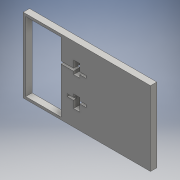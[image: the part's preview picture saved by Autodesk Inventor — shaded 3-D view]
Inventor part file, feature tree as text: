
AUTODESK INVENTOR PART (.ipt)
format: ipt  version: 2016 (Build 200138000, 138)  size: 164,864 bytes
history: native  units: mm
features: extrude x2, sketch x2
ambient origin geometry x8: Origin, YZ Plane, XZ Plane, XY Plane, X Axis, Y Axis, Z Axis, Center Point
bodies: Solid1 (feature_tree)
feature tree (4):
  extrude  "Extrusion1"  Depth=59.0mm
  extrude  "Extrusion2"  Depth=28.0mm
  sketch  "Sketch1"  dims[d0=101.0mm d1=59.0mm]
  sketch  "Sketch2"  dims[d2=2.0mm d3=28.0mm d4=10.0mm d5=5.0mm d6=20.0mm d7=2.0mm d8=10.0mm d9=5.0mm d10=2.0mm d11=0.0mm d12=3.0mm d13=0.0mm]
